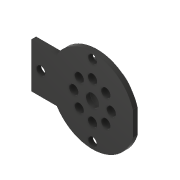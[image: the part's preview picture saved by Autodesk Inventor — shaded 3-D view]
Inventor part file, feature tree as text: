
AUTODESK INVENTOR PART (.ipt)
format: ipt  version: 2017 (Build 210142000, 142)  size: 216,576 bytes
history: native  units: in
note: dims shown in document units (in); Inventor stores cm internally (conversion verified against a paired STEP export)
features: sketch x12, extrude x11, reference x9, other x7, pattern_circular x1
ambient origin geometry x8: Origin, YZ Plane, XZ Plane, XY Plane, X Axis, Y Axis, Z Axis, Center Point
bodies: Solid1 (feature_tree)
feature tree (40):
  extrude  "Extrusion1"  Depth=0.04in
  extrude  "Extrusion2"  Depth=0.3in TaperAngle=0.0deg
  sketch  "Sketch3"  dims[d10=0.0625in d11=0.0in d12=0.12in]
  extrude  "Extrusion4"  Depth=0.0625in
  extrude  "Extrusion5"  Depth=0.0625in
  extrude  "Extrusion6"  Depth=1.0in TaperAngle=0.0deg
  extrude  "Extrusion7"  Depth=0.25in
  extrude  "Extrusion8"  Depth=0.177in
  extrude  "Extrusion9"  Depth=0.15in TaperAngle=0.0deg
  extrude  "Extrusion10"  Depth=0.125in
  extrude  "Extrusion11"  Depth=3.1496in TaperAngle=360.0deg
  extrude  "Extrusion12"  [1 undecoded]
  pattern_circular  "Circular Pattern1"  [2 undecoded]
  sketch  "Sketch1"  dims[d0=0.07in d1=0.04in]
  reference  "Reference1"
  reference  "Reference2"
  sketch  "Sketch2"  dims[d2=0.75in d3=0.0in d4=0.3in d5=0.0in]
  reference  "Reference3"
  sketch  "Sketch5"  dims[d13=0.0625in d14=0.0in d15=0.27in]
  reference  "Reference5"
  sketch  "Sketch6"  dims[d16=1.0in d17=0.0in d18=1.0in d19=0.0in]
  sketch  "Sketch7"  dims[d20=0.5in d21=0.0in d22=0.25in]
  sketch  "Sketch8"  dims[d23=0.3in d24=0.177in]
  reference  "Reference6"
  sketch  "Sketch9"  dims[d25=1.0in d26=0.0in d27=0.15in d28=0.0in]
  reference  "Reference7"
  reference  "Reference8"
  reference  "Reference9"
  reference  "Reference10"
  sketch  "Sketch10"  dims[d29=1.0in d30=0.0in d31=0.125in]
  sketch  "Sketch11"  dims[d32=1.0in d33=0.0in d34=3.1496in d35=360.0deg]
  sketch  "Sketch12"
  sketch  "Sketch13"
  parser-record x1  (decoder bookkeeping rows leaked as tree rows — omitted from the tree; the rows remain in map.json)
  other  "Assembly1.iam"
  other  "Holder copy:1"
  other  ".25 aluminum:1"
  other  "Bottom Assembly:1"
  other  "Led Holder:1"
  other  "Holder copy 2:1"
note: 3 required parameter values undecoded (feature->parameter linkage not recoverable at this tier; creation-order binding heuristic only, values carry confidence <= 0.55)
note: 1 file-system path scrubbed to <path> (originals preserved in map.json)
